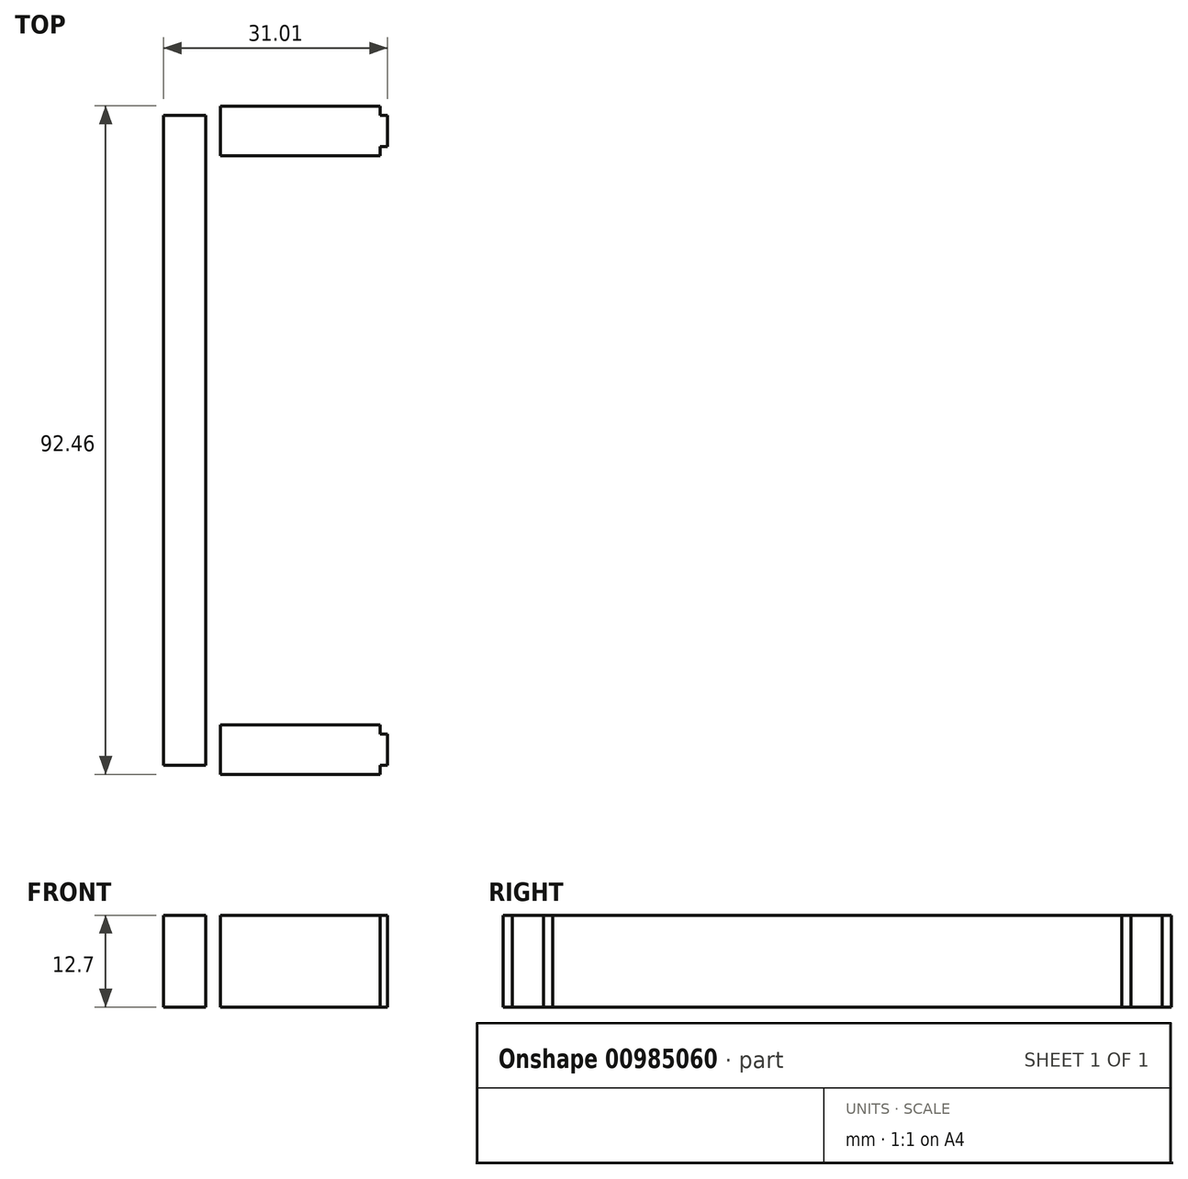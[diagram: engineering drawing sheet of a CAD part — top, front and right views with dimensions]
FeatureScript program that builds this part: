
annotation { "Feature Type Name" : "Feature", "Feature Type Description" : "" }
export const myFeature = defineFeature(function(context is Context, id is Id, definition is map)
    precondition{}
    {
        {
            var Q0;
            Q0=qCreatedBy(makeId("Top.planeOp"),FACE);
            var sketch = newSketch(context, id + "F0", { "sketchPlane" : qUnion([Q0])});
            skLineSegment(sketch, "E0.bottom", {"start": v(-44.97, -50.8) * mm, "end": v(-50.84, -50.8) * mm});
            skLineSegment(sketch, "E0.left", {"start": v(-44.97, -50.8) * mm, "end": v(-44.97, 39.12) * mm});
            skLineSegment(sketch, "E0.right", {"start": v(-50.84, -50.8) * mm, "end": v(-50.84, 39.12) * mm});
            skLineSegment(sketch, "E1.bottom", {"start": v(-44.97, -46.48) * mm, "end": v(-19.83, -46.48) * mm});
            skLineSegment(sketch, "E1.top", {"start": v(-44.97, -50.8) * mm, "end": v(-19.83, -50.8) * mm});
            skLineSegment(sketch, "E1.left", {"start": v(-44.97, -46.48) * mm, "end": v(-44.97, -50.8) * mm});
            skLineSegment(sketch, "E1.right", {"start": v(-19.83, -46.48) * mm, "end": v(-19.83, -50.8) * mm});
            skLineSegment(sketch, "E2.bottom", {"start": v(-42.94, -45.21) * mm, "end": v(-20.84, -45.21) * mm});
            skLineSegment(sketch, "E2.top", {"start": v(-42.94, -52.07) * mm, "end": v(-20.84, -52.07) * mm});
            skLineSegment(sketch, "E2.left", {"start": v(-42.94, -45.21) * mm, "end": v(-42.94, -52.07) * mm});
            skLineSegment(sketch, "E2.right", {"start": v(-20.84, -45.21) * mm, "end": v(-20.84, -52.07) * mm});
            skLineSegment(sketch, "E3", {"start": v(-50.84, 39.12) * mm, "end": v(-44.97, 39.12) * mm});
            skLineSegment(sketch, "E4.MirrorCS", {"start": v(-44.97, 34.8) * mm, "end": v(-44.97, 39.12) * mm});
            skLineSegment(sketch, "E5.MirrorCS", {"start": v(-20.84, 33.53) * mm, "end": v(-20.84, 40.39) * mm});
            skLineSegment(sketch, "E6.MirrorCS", {"start": v(-19.83, 34.8) * mm, "end": v(-19.83, 39.12) * mm});
            skLineSegment(sketch, "E7.MirrorCS", {"start": v(-42.94, 33.53) * mm, "end": v(-42.94, 40.39) * mm});
            skLineSegment(sketch, "E8.MirrorCS", {"start": v(-42.94, 33.53) * mm, "end": v(-20.84, 33.53) * mm});
            skLineSegment(sketch, "E9.MirrorCS", {"start": v(-42.94, 40.39) * mm, "end": v(-20.84, 40.39) * mm});
            skLineSegment(sketch, "E10.MirrorCS", {"start": v(-44.97, 34.8) * mm, "end": v(-19.83, 34.8) * mm});
            skLineSegment(sketch, "E11.MirrorCS", {"start": v(-44.97, 39.12) * mm, "end": v(-19.83, 39.12) * mm});
            skSolve(sketch);
        }
        {
            var Q0;
            {var subQ0=sQuery(id+"F0.wireOp",EDGE,"E2.left");var subQ1=sQuery(id+"F0.wireOp",EDGE,"E1.bottom");var subQ2=makeQuery(id+"F0.imprint","INTERSECT",VERTEX,{"derivedFrom":[subQ1,subQ0]});Q0=makeQuery(id+"F0.imprint","IMPRINT",FACE,{"disambiguationData":[TD([[makeQuery(id+"F0.imprint","IMPRINT",EDGE,{"disambiguationData":[TD([[subQ2,-1.0]])],"derivedFrom":subQ1}),-1.0]])]});}
            var Q1;
            {var subQ0=sQuery(id+"F0.wireOp",EDGE,"E1.left");Q1=makeQuery(id+"F0.imprint","IMPRINT",FACE,{"disambiguationData":[TD([[makeQuery(id+"F0.imprint","IMPRINT",EDGE,{"derivedFrom":subQ0}),1.0]])]});}
            var Q2;
            {var subQ5=sQuery(id+"F0.wireOp",EDGE,"E2.top");Q2=makeQuery(id+"F0.imprint","IMPRINT",FACE,{"disambiguationData":[TD([[makeQuery(id+"F0.imprint","IMPRINT",EDGE,{"derivedFrom":subQ5}),1.0]])]});}
            var Q3;
            {var subQ5=sQuery(id+"F0.wireOp",EDGE,"E2.bottom");Q3=makeQuery(id+"F0.imprint","IMPRINT",FACE,{"disambiguationData":[TD([[makeQuery(id+"F0.imprint","IMPRINT",EDGE,{"derivedFrom":subQ5}),-1.0]])]});}
            var Q4;
            {var subQ0=sQuery(id+"F0.wireOp",EDGE,"E1.right");Q4=makeQuery(id+"F0.imprint","IMPRINT",FACE,{"disambiguationData":[TD([[makeQuery(id+"F0.imprint","IMPRINT",EDGE,{"derivedFrom":subQ0}),-1.0]])]});}
            var Q5;
            Q5=makeQuery(id+"F0.imprint","IMPRINT",FACE,{"disambiguationData":[TD([[makeQuery(id+"F0.imprint","IMPRINT",EDGE,{"derivedFrom":sQuery(id+"F0.wireOp",EDGE,"E0.bottom")}),-1.0]])]});
            var Q6;
            {var subQ5=sQuery(id+"F0.wireOp",EDGE,"4f80d595-9872-43c4-b11e-a619361987873.MirrorCS");Q6=makeQuery(id+"F0.imprint","IMPRINT",FACE,{"disambiguationData":[TD([[makeQuery(id+"F0.imprint","IMPRINT",EDGE,{"derivedFrom":subQ5}),-1.0]])]});}
            var Q7;
            {var subQ0=sQuery(id+"F0.wireOp",EDGE,"4f80d595-9872-43c4-b11e-a619361987877.MirrorCS");var subQ1=sQuery(id+"F0.wireOp",EDGE,"4f80d595-9872-43c4-b11e-a619361987870.MirrorCS");var subQ2=makeQuery(id+"F0.imprint","INTERSECT",VERTEX,{"derivedFrom":[subQ1,subQ0]});Q7=makeQuery(id+"F0.imprint","IMPRINT",FACE,{"disambiguationData":[TD([[makeQuery(id+"F0.imprint","IMPRINT",EDGE,{"disambiguationData":[TD([[subQ2,-1.0]])],"derivedFrom":subQ1}),-1.0]])]});}
            var Q8;
            {var subQ0=sQuery(id+"F0.wireOp",EDGE,"4f80d595-9872-43c4-b11e-a619361987874.MirrorCS");Q8=makeQuery(id+"F0.imprint","IMPRINT",FACE,{"disambiguationData":[TD([[makeQuery(id+"F0.imprint","IMPRINT",EDGE,{"derivedFrom":subQ0}),1.0]])]});}
            var Q9;
            {var subQ0=sQuery(id+"F0.wireOp",EDGE,"4f80d595-9872-43c4-b11e-a619361987875.MirrorCS");Q9=makeQuery(id+"F0.imprint","IMPRINT",FACE,{"disambiguationData":[TD([[makeQuery(id+"F0.imprint","IMPRINT",EDGE,{"derivedFrom":subQ0}),-1.0]])]});}
            var Q10;
            {var subQ5=sQuery(id+"F0.wireOp",EDGE,"4f80d595-9872-43c4-b11e-a619361987872.MirrorCS");Q10=makeQuery(id+"F0.imprint","IMPRINT",FACE,{"disambiguationData":[TD([[makeQuery(id+"F0.imprint","IMPRINT",EDGE,{"derivedFrom":subQ5}),1.0]])]});}
            extrude(context, id + "F1", {"entities" : qUnion([Q0, Q1, Q2, Q3, Q4, Q5, Q6, Q7, Q8, Q9, Q10]), "depth" : 12.7 * mm, "offsetDistance" : 25.4 * mm});
        }
        {
            var Q0;
            {var subQ0=sQuery(id+"F0.wireOp",EDGE,"E10.MirrorCS");var subQ1=sQuery(id+"F0.wireOp",EDGE,"E5.MirrorCS");var subQ2=makeQuery(id+"F0.imprint","INTERSECT",VERTEX,{"derivedFrom":[subQ1,subQ0]});Q0=makeQuery(id+"F0.imprint","IMPRINT",FACE,{"disambiguationData":[TD([[makeQuery(id+"F0.imprint","IMPRINT",EDGE,{"disambiguationData":[TD([[subQ2,-1.0]])],"derivedFrom":subQ1}),1.0]])]});}
            var Q1;
            {var subQ0=sQuery(id+"F0.wireOp",EDGE,"E4.MirrorCS");Q1=makeQuery(id+"F0.imprint","IMPRINT",FACE,{"disambiguationData":[TD([[makeQuery(id+"F0.imprint","IMPRINT",EDGE,{"derivedFrom":subQ0}),-1.0]])]});}
            var Q2;
            {var subQ0=sQuery(id+"F0.wireOp",EDGE,"E8.MirrorCS");Q2=makeQuery(id+"F0.imprint","IMPRINT",FACE,{"disambiguationData":[TD([[makeQuery(id+"F0.imprint","IMPRINT",EDGE,{"derivedFrom":subQ0}),1.0]])]});}
            var Q3;
            {var subQ0=sQuery(id+"F0.wireOp",EDGE,"E9.MirrorCS");Q3=makeQuery(id+"F0.imprint","IMPRINT",FACE,{"disambiguationData":[TD([[makeQuery(id+"F0.imprint","IMPRINT",EDGE,{"derivedFrom":subQ0}),-1.0]])]});}
            var Q4;
            {var subQ5=sQuery(id+"F0.wireOp",EDGE,"E6.MirrorCS");Q4=makeQuery(id+"F0.imprint","IMPRINT",FACE,{"disambiguationData":[TD([[makeQuery(id+"F0.imprint","IMPRINT",EDGE,{"derivedFrom":subQ5}),1.0]])]});}
            extrude(context, id + "F2", {"entities" : qUnion([Q0, Q1, Q2, Q3, Q4]), "operationType" : NewBodyOperationType.ADD, "depth" : 12.7 * mm, "offsetDistance" : 25.4 * mm});
        }
    });
